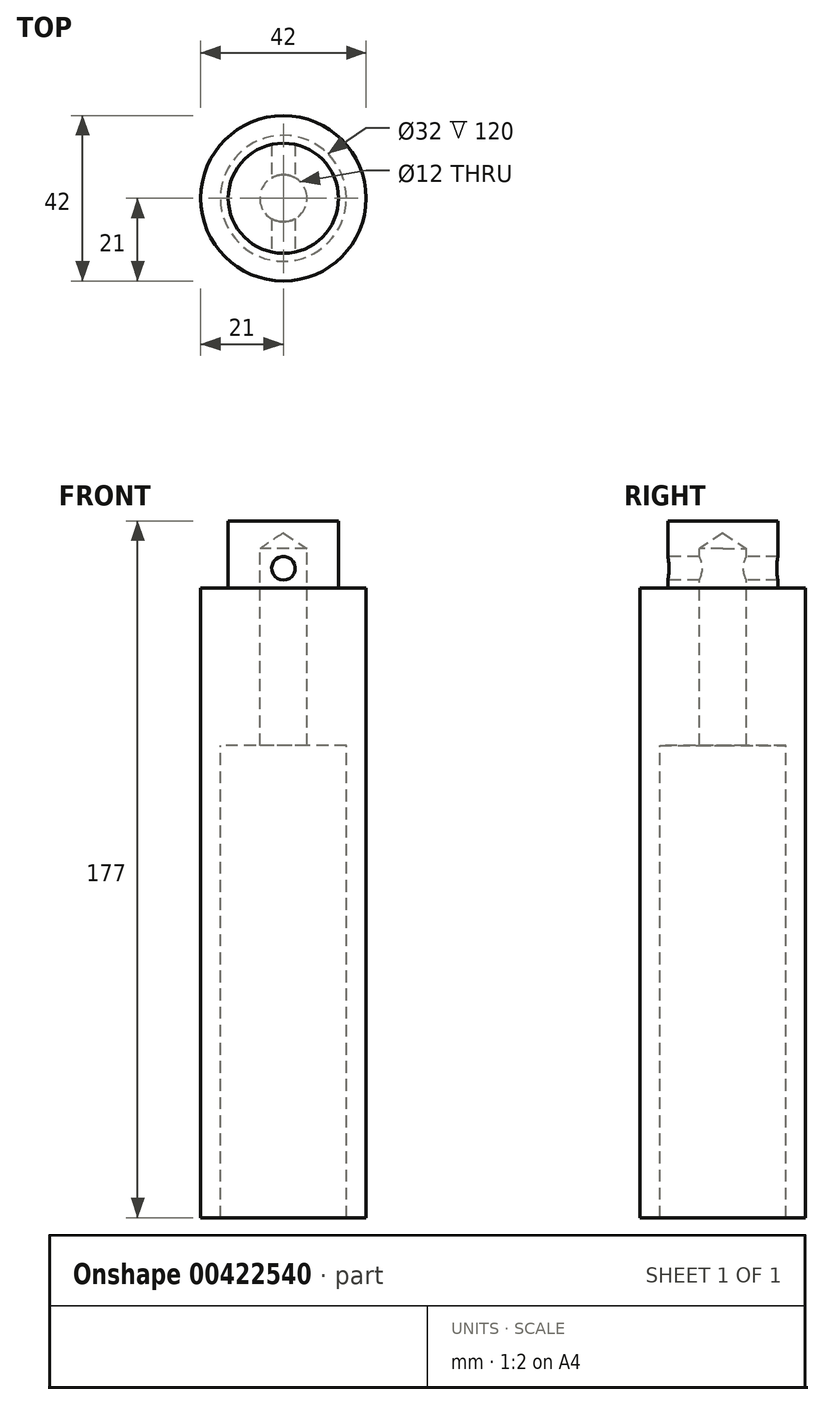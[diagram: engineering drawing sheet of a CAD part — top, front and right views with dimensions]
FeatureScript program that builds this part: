
annotation { "Feature Type Name" : "Feature", "Feature Type Description" : "" }
export const myFeature = defineFeature(function(context is Context, id is Id, definition is map)
    precondition{}
    {
        {
            var Q0;
            Q0=qCreatedBy(makeId("Front.planeOp"),FACE);
            var sketch = newSketch(context, id + "F0", { "sketchPlane" : qUnion([Q0])});
            skLineSegment(sketch, "E0", {"start": v(0, 53.56) * mm, "end": v(0, -55.93) * mm, "construction": true});
            skLineSegment(sketch, "E1", {"start": v(0, -32.88) * mm, "end": v(16, -32.88) * mm, "construction": true});
            skLineSegment(sketch, "E2", {"start": v(16, -32.88) * mm, "end": v(21, -32.88) * mm, "construction": true});
            skLineSegment(sketch, "E3", {"start": v(16, -72.83) * mm, "end": v(21, -72.83) * mm});
            skLineSegment(sketch, "E4", {"start": v(21, -72.83) * mm, "end": v(21, 87.17) * mm});
            skLineSegment(sketch, "E5", {"start": v(16, -72.83) * mm, "end": v(16, 47.17) * mm});
            skLineSegment(sketch, "E6", {"start": v(16, 47.17) * mm, "end": v(6, 47.17) * mm});
            skLineSegment(sketch, "E7", {"start": v(21, 87.17) * mm, "end": v(14, 87.17) * mm});
            skLineSegment(sketch, "E8", {"start": v(14, 87.17) * mm, "end": v(14, 97.17) * mm});
            skLineSegment(sketch, "E9", {"start": v(6, 47.17) * mm, "end": v(6, 97.17) * mm});
            skLineSegment(sketch, "E10", {"start": v(14, 97.17) * mm, "end": v(14, 104.17) * mm});
            skLineSegment(sketch, "E11", {"start": v(14, 104.17) * mm, "end": v(0, 104.17) * mm});
            skLineSegment(sketch, "E12", {"start": v(0, 104.17) * mm, "end": v(0, 101.17) * mm});
            skLineSegment(sketch, "E13", {"start": v(0, 101.17) * mm, "end": v(6, 97.17) * mm});
            skSolve(sketch);
        }
        {
            var Q0;
            Q0=makeQuery(id+"F0.imprint","IMPRINT",FACE,{"disambiguationData":[TD([[makeQuery(id+"F0.imprint","IMPRINT",EDGE,{"derivedFrom":sQuery(id+"F0.wireOp",EDGE,"E3")}),1.0]])]});
            var Q1;
            Q1=sQuery(id+"F0.wireOp",EDGE,"E0");
            revolve(context, id + "F1", {"entities" : qUnion([Q0]), "axis" : qUnion([Q1]), "revolveType" : RevolveType.FULL});
        }
        {
            var Q0;
            Q0=qCreatedBy(makeId("Front.planeOp"),FACE);
            var sketch = newSketch(context, id + "F2", { "sketchPlane" : qUnion([Q0])});
            skLineSegment(sketch, "E14", {"start": v(-14, 87.17) * mm, "end": v(-14, 104.17) * mm, "construction": true});
            skLineSegment(sketch, "E15", {"start": v(14, 104.17) * mm, "end": v(14, 87.17) * mm, "construction": true});
            skLineSegment(sketch, "E16", {"start": v(-14, 87.17) * mm, "end": v(-14, 97.17) * mm, "construction": true});
            skLineSegment(sketch, "E17", {"start": v(-14, 97.17) * mm, "end": v(14, 97.17) * mm, "construction": true});
            skLineSegment(sketch, "E18", {"start": v(-14, 87.17) * mm, "end": v(14, 87.17) * mm, "construction": true});
            skLineSegment(sketch, "E19", {"start": v(0, 97.17) * mm, "end": v(0, 87.17) * mm, "construction": true});
            skCircle(sketch, "E20", {"center": v(0, 92.17) * mm, "radius": 3 * mm});
            skSolve(sketch);
        }
        {
            var Q0;
            Q0 = qSketchRegion(id + "F2", true);
            extrude(context, id + "F3", {"entities" : qUnion([Q0]), "operationType" : NewBodyOperationType.REMOVE, "endBound" : BoundingType.SYMMETRIC, "oppositeDirection" : true, "depth" : 50 * mm});
        }
    });
